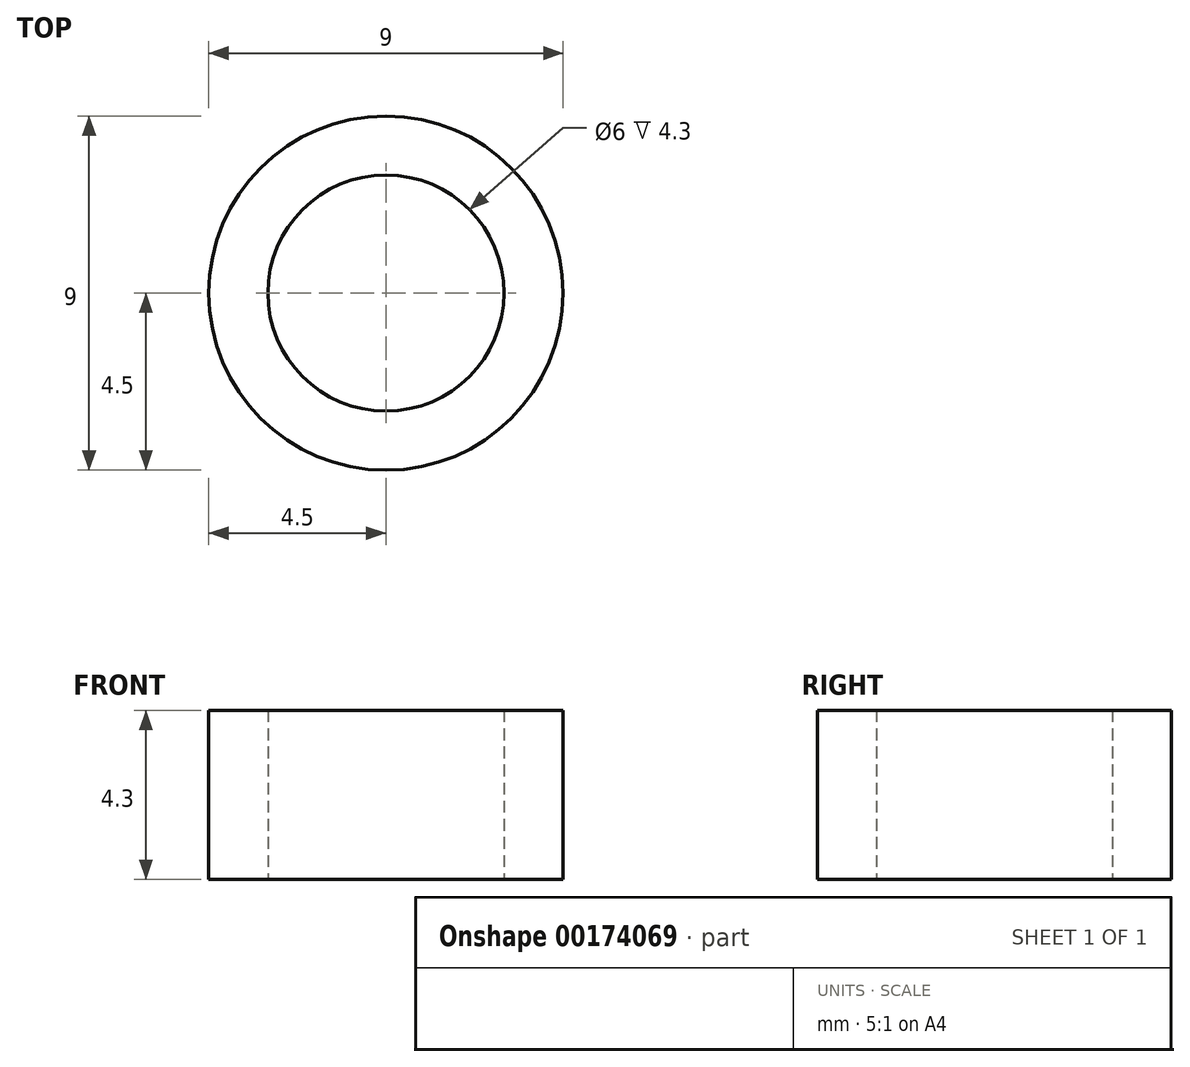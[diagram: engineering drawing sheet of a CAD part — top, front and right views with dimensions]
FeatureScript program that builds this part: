
annotation { "Feature Type Name" : "Feature", "Feature Type Description" : "" }
export const myFeature = defineFeature(function(context is Context, id is Id, definition is map)
    precondition{}
    {
        {
            var Q0;
            Q0=qCreatedBy(makeId("Top.planeOp"),FACE);
            var sketch = newSketch(context, id + "F0", { "sketchPlane" : qUnion([Q0])});
            skCircle(sketch, "E0", {"center": v(0, 0) * mm, "radius": 4.5 * mm});
            skCircle(sketch, "E1", {"center": v(0, 0) * mm, "radius": 3 * mm});
            skSolve(sketch);
        }
        {
            var Q0;
            Q0=makeQuery(id+"F0.imprint","IMPRINT",FACE,{"disambiguationData":[TD([[makeQuery(id+"F0.imprint","IMPRINT",EDGE,{"derivedFrom":sQuery(id+"F0.wireOp",EDGE,"E0")}),1.0]])]});
            extrude(context, id + "F1", {"entities" : qUnion([Q0]), "depth" : 4.3 * mm});
        }
    });
